# Revit family: FantiniCosmi_BIM_C50C
name_source: partatom
category: Modelli generici
units: mm (PartAtom-declared; Revit-internal decimal feet)

## family parameters
Basato su piano di lavoro = No
Condiviso = No
Punto di calcolo locali = No
Può ospitare armatura = No
Quota connettore circolare = Usa diametro
Sempre verticale = Sì
Taglio con vuoti quando caricato = No
Tipo di parte = Normale

## types (1)
- Standard
    Body admissible temperature = - 10 ÷ 50 °C
    Catalog web link = https://www.fantinicosmi.it
    Color = Silver
    Descrizione = Flush-mounting room thermostat, with batteries, 2 temperature levels
    Design Status = 1
    Fixed antifreeze temperature = 8°C
    Part Number = FantiniCosmi_BIM_C50C
    Power supply = 3 batteries AAA 1,5V
    Prospetto di default = 0 mm  [stored 0 ft]
    Protection degree = IP20
    Temperature regulation range = 8 ÷ 40 °C
    Unit weight = 0.13 Kg

note: [stored X ft] marks values corroborated as IEEE doubles in the binary element streams (Revit-internal decimal feet)

## geometry (parser evidence)
native form markers: Sweep x3
no freeform markers — native parametric forms only
